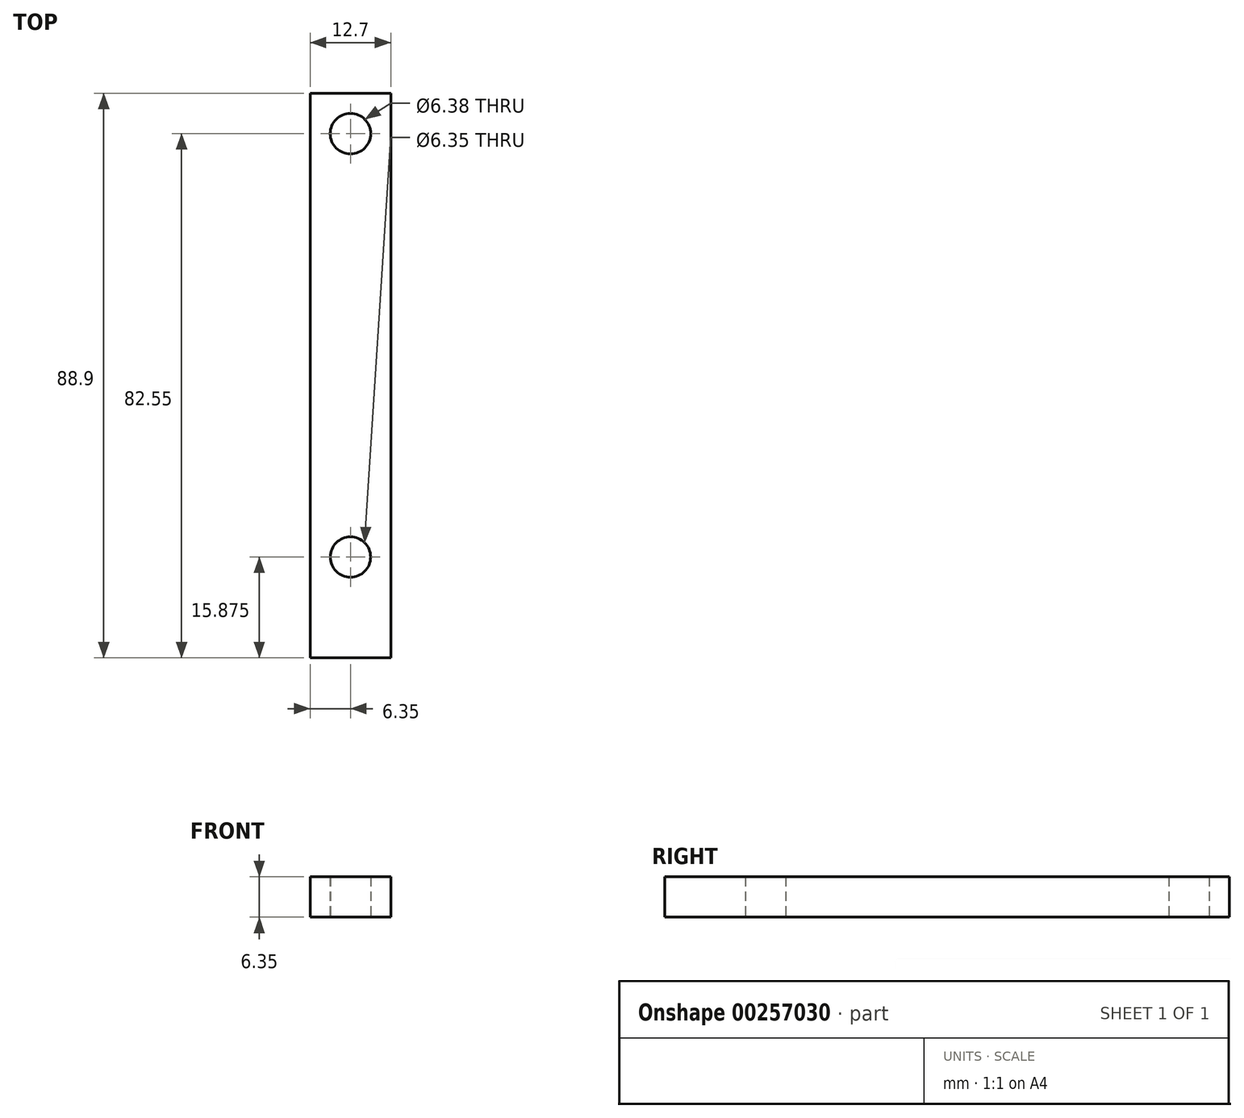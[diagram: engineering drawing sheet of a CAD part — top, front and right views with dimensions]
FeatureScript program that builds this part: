
annotation { "Feature Type Name" : "Feature", "Feature Type Description" : "" }
export const myFeature = defineFeature(function(context is Context, id is Id, definition is map)
    precondition{}
    {
        {
            var Q0;
            Q0=qCreatedBy(makeId("Top.planeOp"),FACE);
            var sketch = newSketch(context, id + "F0", { "sketchPlane" : qUnion([Q0])});
            skLineSegment(sketch, "E0.bottom", {"start": v(6.35, 44.45) * mm, "end": v(-6.35, 44.45) * mm});
            skLineSegment(sketch, "E0.top", {"start": v(6.35, -44.45) * mm, "end": v(-6.35, -44.45) * mm});
            skLineSegment(sketch, "E0.left", {"start": v(6.35, 44.45) * mm, "end": v(6.35, -44.45) * mm});
            skLineSegment(sketch, "E0.right", {"start": v(-6.35, 44.45) * mm, "end": v(-6.35, -44.45) * mm});
            skPoint(sketch, "E0.middle", {"position": v(0, 0) * mm});
            skCircle(sketch, "E1", {"center": v(0, 38.1) * mm, "radius": 3.19 * mm});
            skCircle(sketch, "E2", {"center": v(0, -28.58) * mm, "radius": 3.18 * mm});
            skSolve(sketch);
        }
        {
            var Q0;
            Q0 = qSketchRegion(id + "F0", true);
            extrude(context, id + "F1", {"entities" : qUnion([Q0]), "depth" : 6.35 * mm});
        }
    });
